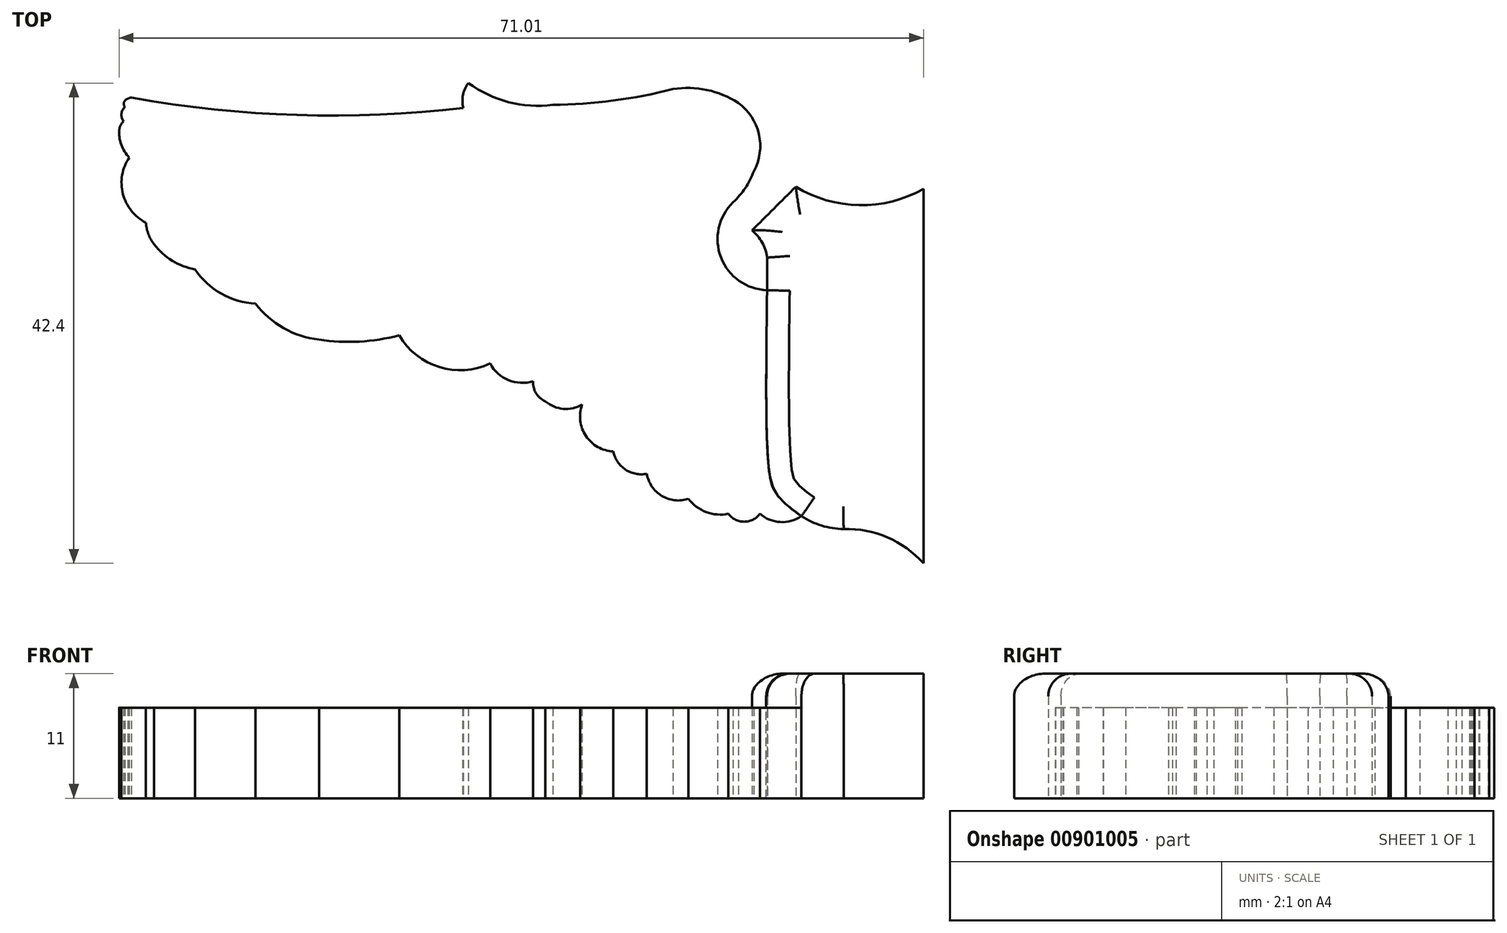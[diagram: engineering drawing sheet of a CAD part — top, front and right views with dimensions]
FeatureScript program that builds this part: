
annotation { "Feature Type Name" : "Feature", "Feature Type Description" : "" }
export const myFeature = defineFeature(function(context is Context, id is Id, definition is map)
    precondition{}
    {
        {
            var Q0;
            Q0=qCreatedBy(makeId("Top.planeOp"),FACE);
            var sketch = newSketch(context, id + "F0", { "sketchPlane" : qUnion([Q0])});
            skArc(sketch, "E0", {"start": v(-69.93, 44.49) * mm, "mid": v(-55.31, 42.96) * mm, "end": v(-40.63, 43.58) * mm});
            skArc(sketch, "E1", {"start": v(-40.18, 45.78) * mm, "mid": v(-40.65, 44.73) * mm, "end": v(-40.63, 43.58) * mm});
            skArc(sketch, "E2", {"start": v(-40.18, 45.78) * mm, "mid": v(-36.64, 44.1) * mm, "end": v(-32.72, 43.85) * mm});
            skPoint(sketch, "E3", {"position": v(-38.48, 44.77) * mm});
            skPoint(sketch, "E4", {"position": v(-36.75, 44.13) * mm});
            skArc(sketch, "E5", {"start": v(-32.72, 43.85) * mm, "mid": v(-27.37, 44.24) * mm, "end": v(-22.1, 45.25) * mm});
            skArc(sketch, "E6", {"start": v(-16.8, 35.25) * mm, "mid": v(-15.7, 36.55) * mm, "end": v(-14.94, 38.08) * mm});
            skArc(sketch, "E7", {"start": v(-16.8, 35.25) * mm, "mid": v(-17.87, 30.37) * mm, "end": v(-13.8, 27.49) * mm});
            skArc(sketch, "E8", {"start": v(-13.8, 27.49) * mm, "mid": v(-13.78, 28.93) * mm, "end": v(-13.8, 30.37) * mm});
            skArc(sketch, "E9", {"start": v(-13.8, 30.37) * mm, "mid": v(-14.24, 31.7) * mm, "end": v(-15.14, 32.77) * mm});
            skArc(sketch, "E10", {"start": v(-15.14, 32.77) * mm, "mid": v(-13.2, 34.7) * mm, "end": v(-11.27, 36.63) * mm});
            skArc(sketch, "E11", {"start": v(0.26, 36.63) * mm, "mid": v(0.13, 36.69) * mm, "end": v(0, 36.63) * mm});
            skPoint(sketch, "E12", {"position": v(-34.14, 43.77) * mm});
            skPoint(sketch, "E13", {"position": v(-32.83, 43.84) * mm});
            skPoint(sketch, "E14", {"position": v(-31.45, 44.1) * mm});
            skPoint(sketch, "E15", {"position": v(-35.62, 43.9) * mm});
            skPoint(sketch, "E16", {"position": v(-18.6, 45.35) * mm});
            skPoint(sketch, "E17", {"position": v(-17.41, 44.84) * mm});
            skArc(sketch, "E18", {"start": v(-11.27, 36.63) * mm, "mid": v(-5.58, 35) * mm, "end": v(0.13, 36.52) * mm});
            skLineSegment(sketch, "E19", {"start": v(0, 36.63) * mm, "end": v(0, 3.38) * mm});
            skArc(sketch, "E20", {"start": v(0, 3.38) * mm, "mid": v(-3.19, 5.67) * mm, "end": v(-7.05, 6.4) * mm});
            skArc(sketch, "E21", {"start": v(-10.77, 7.53) * mm, "mid": v(-9, 6.7) * mm, "end": v(-7.05, 6.4) * mm});
            skArc(sketch, "E22", {"start": v(-14.44, 7.75) * mm, "mid": v(-12.64, 7.02) * mm, "end": v(-10.77, 7.53) * mm});
            skArc(sketch, "E23", {"start": v(-17.22, 7.75) * mm, "mid": v(-15.83, 7.05) * mm, "end": v(-14.44, 7.75) * mm});
            skArc(sketch, "E24", {"start": v(-20.75, 9.07) * mm, "mid": v(-19.18, 7.9) * mm, "end": v(-17.22, 7.75) * mm});
            skArc(sketch, "E25", {"start": v(-24.42, 11.28) * mm, "mid": v(-23.1, 9.32) * mm, "end": v(-20.75, 9.07) * mm});
            skArc(sketch, "E26", {"start": v(-27.39, 13.25) * mm, "mid": v(-26.31, 11.65) * mm, "end": v(-24.42, 11.28) * mm});
            skArc(sketch, "E27", {"start": v(-30.14, 17.38) * mm, "mid": v(-29.8, 14.62) * mm, "end": v(-27.39, 13.25) * mm});
            skArc(sketch, "E28", {"start": v(-33.37, 17.68) * mm, "mid": v(-31.8, 17.01) * mm, "end": v(-30.14, 17.38) * mm});
            skArc(sketch, "E29", {"start": v(-34.45, 19.46) * mm, "mid": v(-34.2, 18.4) * mm, "end": v(-33.37, 17.68) * mm});
            skArc(sketch, "E30", {"start": v(-38.26, 21.02) * mm, "mid": v(-36.64, 19.55) * mm, "end": v(-34.45, 19.46) * mm});
            skArc(sketch, "E31", {"start": v(-46.3, 23.5) * mm, "mid": v(-42.76, 20.7) * mm, "end": v(-38.26, 21.02) * mm});
            skArc(sketch, "E32", {"start": v(-53.36, 23.13) * mm, "mid": v(-49.8, 22.95) * mm, "end": v(-46.3, 23.5) * mm});
            skArc(sketch, "E33", {"start": v(-58.97, 26.3) * mm, "mid": v(-56.5, 24.15) * mm, "end": v(-53.36, 23.13) * mm});
            skArc(sketch, "E34", {"start": v(-64.31, 29.33) * mm, "mid": v(-62, 27.18) * mm, "end": v(-58.97, 26.3) * mm});
            skArc(sketch, "E35", {"start": v(-67.93, 31.54) * mm, "mid": v(-66.33, 30.1) * mm, "end": v(-64.31, 29.33) * mm});
            skArc(sketch, "E36", {"start": v(-68.65, 33.46) * mm, "mid": v(-68.43, 32.45) * mm, "end": v(-67.93, 31.54) * mm});
            skArc(sketch, "E37", {"start": v(-70.11, 39.2) * mm, "mid": v(-70.68, 36) * mm, "end": v(-68.65, 33.46) * mm});
            skArc(sketch, "E38", {"start": v(-71, 41.69) * mm, "mid": v(-70.83, 40.35) * mm, "end": v(-70.11, 39.2) * mm});
            skArc(sketch, "E39", {"start": v(-70.62, 42.41) * mm, "mid": v(-70.87, 42.08) * mm, "end": v(-71, 41.69) * mm});
            skArc(sketch, "E40", {"start": v(-70.5, 43.66) * mm, "mid": v(-70.81, 43.06) * mm, "end": v(-70.62, 42.41) * mm});
            skArc(sketch, "E41", {"start": v(-70.23, 44.4) * mm, "mid": v(-70.57, 44.1) * mm, "end": v(-70.5, 43.66) * mm});
            skArc(sketch, "E42", {"start": v(-69.93, 44.49) * mm, "mid": v(-70.1, 44.47) * mm, "end": v(-70.23, 44.4) * mm});
            skArc(sketch, "E43", {"start": v(-16.35, 44.03) * mm, "mid": v(-19.12, 45.17) * mm, "end": v(-22.1, 45.25) * mm});
            skArc(sketch, "E44", {"start": v(-14.98, 37.98) * mm, "mid": v(-14.53, 41.27) * mm, "end": v(-16.35, 44.03) * mm});
            skArc(sketch, "E45.MirrorCS", {"start": v(70.23, 44.4) * mm, "mid": v(70.57, 44.1) * mm, "end": v(70.5, 43.66) * mm});
            skArc(sketch, "E46.MirrorCS", {"start": v(69.93, 44.49) * mm, "mid": v(70.1, 44.47) * mm, "end": v(70.23, 44.4) * mm});
            skArc(sketch, "E47.MirrorCS", {"start": v(-0.26, 36.63) * mm, "mid": v(-0.13, 36.69) * mm, "end": v(0, 36.63) * mm});
            skArc(sketch, "E48.MirrorCS", {"start": v(70.5, 43.66) * mm, "mid": v(70.81, 43.06) * mm, "end": v(70.62, 42.41) * mm});
            skArc(sketch, "E49.MirrorCS", {"start": v(68.65, 33.46) * mm, "mid": v(68.43, 32.45) * mm, "end": v(67.93, 31.54) * mm});
            skArc(sketch, "E50.MirrorCS", {"start": v(40.18, 45.78) * mm, "mid": v(40.65, 44.73) * mm, "end": v(40.63, 43.58) * mm});
            skArc(sketch, "E51.MirrorCS", {"start": v(71, 41.69) * mm, "mid": v(70.83, 40.35) * mm, "end": v(70.11, 39.2) * mm});
            skArc(sketch, "E52.MirrorCS", {"start": v(13.8, 30.37) * mm, "mid": v(14.24, 31.7) * mm, "end": v(15.14, 32.77) * mm});
            skArc(sketch, "E53.MirrorCS", {"start": v(10.77, 7.53) * mm, "mid": v(9, 6.7) * mm, "end": v(7.05, 6.4) * mm});
            skArc(sketch, "E54.MirrorCS", {"start": v(20.75, 9.07) * mm, "mid": v(19.18, 7.9) * mm, "end": v(17.22, 7.75) * mm});
            skArc(sketch, "E55.MirrorCS", {"start": v(15.14, 32.77) * mm, "mid": v(13.2, 34.7) * mm, "end": v(11.27, 36.63) * mm});
            skArc(sketch, "E56.MirrorCS", {"start": v(70.62, 42.41) * mm, "mid": v(70.87, 42.08) * mm, "end": v(71, 41.69) * mm});
            skArc(sketch, "E57.MirrorCS", {"start": v(67.93, 31.54) * mm, "mid": v(66.33, 30.1) * mm, "end": v(64.31, 29.33) * mm});
            skArc(sketch, "E58.MirrorCS", {"start": v(13.8, 27.49) * mm, "mid": v(13.78, 28.93) * mm, "end": v(13.8, 30.37) * mm});
            skArc(sketch, "E59.MirrorCS", {"start": v(38.26, 21.02) * mm, "mid": v(36.64, 19.55) * mm, "end": v(34.45, 19.46) * mm});
            skArc(sketch, "E60.MirrorCS", {"start": v(40.18, 45.78) * mm, "mid": v(36.64, 44.1) * mm, "end": v(32.72, 43.85) * mm});
            skArc(sketch, "E61.MirrorCS", {"start": v(17.22, 7.75) * mm, "mid": v(15.83, 7.05) * mm, "end": v(14.44, 7.75) * mm});
            skArc(sketch, "E62.MirrorCS", {"start": v(33.37, 17.68) * mm, "mid": v(31.8, 17.01) * mm, "end": v(30.14, 17.38) * mm});
            skArc(sketch, "E63.MirrorCS", {"start": v(14.44, 7.75) * mm, "mid": v(12.64, 7.02) * mm, "end": v(10.77, 7.53) * mm});
            skArc(sketch, "E64.MirrorCS", {"start": v(34.45, 19.46) * mm, "mid": v(34.2, 18.4) * mm, "end": v(33.37, 17.68) * mm});
            skArc(sketch, "E65.MirrorCS", {"start": v(16.8, 35.25) * mm, "mid": v(15.7, 36.55) * mm, "end": v(14.94, 38.08) * mm});
            skArc(sketch, "E66.MirrorCS", {"start": v(27.39, 13.25) * mm, "mid": v(26.31, 11.65) * mm, "end": v(24.42, 11.28) * mm});
            skPoint(sketch, "E67.MirrorP", {"position": v(35.62, 43.9) * mm});
            skArc(sketch, "E68.MirrorCS", {"start": v(16.35, 44.03) * mm, "mid": v(19.12, 45.17) * mm, "end": v(22.1, 45.25) * mm});
            skArc(sketch, "E69.MirrorCS", {"start": v(11.27, 36.63) * mm, "mid": v(5.58, 35) * mm, "end": v(-0.13, 36.52) * mm});
            skArc(sketch, "E70.MirrorCS", {"start": v(69.93, 44.49) * mm, "mid": v(55.31, 42.96) * mm, "end": v(40.63, 43.58) * mm});
            skPoint(sketch, "E71.MirrorP", {"position": v(36.75, 44.13) * mm});
            skArc(sketch, "E72.MirrorCS", {"start": v(46.3, 23.5) * mm, "mid": v(42.76, 20.7) * mm, "end": v(38.26, 21.02) * mm});
            skArc(sketch, "E73.MirrorCS", {"start": v(70.11, 39.2) * mm, "mid": v(70.68, 36) * mm, "end": v(68.65, 33.46) * mm});
            skArc(sketch, "E74.MirrorCS", {"start": v(14.98, 37.98) * mm, "mid": v(14.53, 41.27) * mm, "end": v(16.35, 44.03) * mm});
            skArc(sketch, "E75.MirrorCS", {"start": v(0, 3.38) * mm, "mid": v(3.19, 5.67) * mm, "end": v(7.05, 6.4) * mm});
            skPoint(sketch, "E76.MirrorP", {"position": v(18.6, 45.35) * mm});
            skPoint(sketch, "E77.MirrorP", {"position": v(31.45, 44.1) * mm});
            skPoint(sketch, "E78.MirrorP", {"position": v(34.14, 43.77) * mm});
            skArc(sketch, "E79.MirrorCS", {"start": v(24.42, 11.28) * mm, "mid": v(23.1, 9.32) * mm, "end": v(20.75, 9.07) * mm});
            skArc(sketch, "E80.MirrorCS", {"start": v(58.97, 26.3) * mm, "mid": v(56.5, 24.15) * mm, "end": v(53.36, 23.13) * mm});
            skArc(sketch, "E81.MirrorCS", {"start": v(53.36, 23.13) * mm, "mid": v(49.8, 22.95) * mm, "end": v(46.3, 23.5) * mm});
            skPoint(sketch, "E82.MirrorP", {"position": v(17.41, 44.84) * mm});
            skArc(sketch, "E83.MirrorCS", {"start": v(16.8, 35.25) * mm, "mid": v(17.87, 30.37) * mm, "end": v(13.8, 27.49) * mm});
            skPoint(sketch, "E84.MirrorP", {"position": v(38.48, 44.77) * mm});
            skPoint(sketch, "E85.MirrorP", {"position": v(32.83, 43.84) * mm});
            skArc(sketch, "E86.MirrorCS", {"start": v(30.14, 17.38) * mm, "mid": v(29.8, 14.62) * mm, "end": v(27.39, 13.25) * mm});
            skArc(sketch, "E87.MirrorCS", {"start": v(32.72, 43.85) * mm, "mid": v(27.37, 44.24) * mm, "end": v(22.1, 45.25) * mm});
            skArc(sketch, "E88.MirrorCS", {"start": v(64.31, 29.33) * mm, "mid": v(62, 27.18) * mm, "end": v(58.97, 26.3) * mm});
            skPoint(sketch, "E89", {"position": v(-13.68, 11.99) * mm});
            skPoint(sketch, "E90", {"position": v(-12.87, 9.36) * mm});
            skPoint(sketch, "E91", {"position": v(-10.77, 7.53) * mm});
            skPoint(sketch, "E92", {"position": v(10.77, 7.53) * mm});
            skPoint(sketch, "E93", {"position": v(13.1, 9.28) * mm});
            skPoint(sketch, "E94", {"position": v(13.98, 12.48) * mm});
            skFitSpline(sketch, "E95", {"points": [v(-13.8, 27.49) * mm, v(-13.68, 11.99) * mm, v(-12.87, 9.36) * mm, v(-10.77, 7.53) * mm], "startDerivative": vector(-0.44, -34.5) * mm, "endDerivative": vector(10.5, -7.67) * mm});
            skFitSpline(sketch, "E96", {"points": [v(13.8, 27.49) * mm, v(13.98, 12.48) * mm, v(13.1, 9.28) * mm, v(10.77, 7.53) * mm], "startDerivative": vector(1.12, -33.73) * mm, "endDerivative": vector(-11.6, -6.84) * mm});
            skSolve(sketch);
        }
        {
            var Q0;
            Q0=makeQuery(id+"F0.imprint","IMPRINT",FACE,{"disambiguationData":[TD([[makeQuery(id+"F0.imprint","IMPRINT",EDGE,{"derivedFrom":sQuery(id+"F0.wireOp",EDGE,"E0")}),-1.0]])]});
            var Q1;
            Q1=makeQuery(id+"F0.imprint","IMPRINT",FACE,{"disambiguationData":[TD([[makeQuery(id+"F0.imprint","IMPRINT",EDGE,{"derivedFrom":sQuery(id+"F0.wireOp",EDGE,"E45.MirrorCS")}),-1.0]])]});
            extrude(context, id + "F1", {"entities" : qUnion([Q0, Q1]), "depth" : 8 * mm, "offsetDistance" : 25 * mm});
        }
        {
            var Q0;
            Q0=makeQuery(id+"F0.imprint","IMPRINT",FACE,{"disambiguationData":[TD([[makeQuery(id+"F0.imprint","IMPRINT",EDGE,{"derivedFrom":sQuery(id+"F0.wireOp",EDGE,"E8")}),-1.0]])]});
            var Q1;
            Q1=makeQuery(id+"F0.imprint","IMPRINT",FACE,{"disambiguationData":[TD([[makeQuery(id+"F0.imprint","IMPRINT",EDGE,{"derivedFrom":sQuery(id+"F0.wireOp",EDGE,"E52.MirrorCS")}),1.0]])]});
            extrude(context, id + "F2", {"entities" : qUnion([Q0, Q1]), "depth" : 11 * mm, "offsetDistance" : 25 * mm});
        }
        {
            var Q0;
            Q0=makeQuery(id+"F2.opExtrude","CAP_EDGE",EDGE,{"disambiguationData":[OSD([sQuery(id+"F0.wireOp",EDGE,"E10")])],"isStart":false});
            var Q1;
            Q1=makeQuery(id+"F2.opExtrude","CAP_EDGE",EDGE,{"disambiguationData":[OSD([sQuery(id+"F0.wireOp",EDGE,"E9")])],"isStart":false});
            var Q2;
            Q2=makeQuery(id+"F2.opExtrude","CAP_EDGE",EDGE,{"disambiguationData":[OSD([sQuery(id+"F0.wireOp",EDGE,"E8")])],"isStart":false});
            var Q3;
            Q3=makeQuery(id+"F2.opExtrude","CAP_EDGE",EDGE,{"disambiguationData":[OSD([sQuery(id+"F0.wireOp",EDGE,"E95")])],"isStart":false});
            var Q4;
            Q4=makeQuery(id+"F2.opExtrude","CAP_EDGE",EDGE,{"disambiguationData":[OSD([sQuery(id+"F0.wireOp",EDGE,"E20")])],"isStart":false});
            var Q5;
            Q5=makeQuery(id+"F2.opExtrude","CAP_EDGE",EDGE,{"disambiguationData":[OSD([sQuery(id+"F0.wireOp",EDGE,"E75.MirrorCS")])],"isStart":false});
            var Q6;
            Q6=makeQuery(id+"F2.opExtrude","CAP_EDGE",EDGE,{"disambiguationData":[OSD([sQuery(id+"F0.wireOp",EDGE,"E53.MirrorCS")])],"isStart":false});
            var Q7;
            Q7=makeQuery(id+"F2.opExtrude","CAP_EDGE",EDGE,{"disambiguationData":[OSD([sQuery(id+"F0.wireOp",EDGE,"E96")])],"isStart":false});
            var Q8;
            Q8=makeQuery(id+"F2.opExtrude","CAP_EDGE",EDGE,{"disambiguationData":[OSD([sQuery(id+"F0.wireOp",EDGE,"E55.MirrorCS")])],"isStart":false});
            var Q9;
            Q9=makeQuery(id+"F2.opExtrude","CAP_EDGE",EDGE,{"disambiguationData":[OSD([sQuery(id+"F0.wireOp",EDGE,"E69.MirrorCS")])],"isStart":false});
            var Q10;
            Q10=makeQuery(id+"F2.opExtrude","CAP_EDGE",EDGE,{"disambiguationData":[OSD([sQuery(id+"F0.wireOp",EDGE,"E18")])],"isStart":false});
            fillet(context, id + "F3", {"entities" : qUnion([Q0, Q1, Q2, Q3, Q4, Q5, Q6, Q7, Q8, Q9, Q10]), "radius" : 2 * mm, "tangentPropagation" : true, "allowEdgeOverflow" : false});
        }
    });
